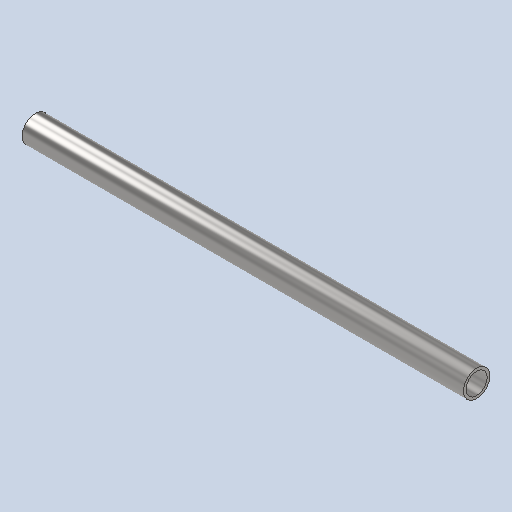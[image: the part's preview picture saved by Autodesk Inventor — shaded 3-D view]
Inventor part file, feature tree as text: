
AUTODESK INVENTOR PART (.ipt)
format: ipt  version: 2022 (Build 260153000, 153)  size: 128,000 bytes
history: native  units: in
note: dims shown in document units (in); Inventor stores cm internally (conversion verified against a paired STEP export)
features: extrude x2, sketch x1
ambient origin geometry x8: Origin, YZ Plane, XZ Plane, XY Plane, X Axis, Y Axis, Z Axis, Center Point
bodies: Solid1 (feature_tree)
feature tree (3):
  extrude  "Extrusion1"  [1 undecoded]
  sketch  "Sketch1"  dims[d0=22.0in d1=0.0in]
  extrude  "Extrude1"  [1 undecoded]
note: 2 required parameter values undecoded (feature->parameter linkage not recoverable at this tier; creation-order binding heuristic only, values carry confidence <= 0.55)
